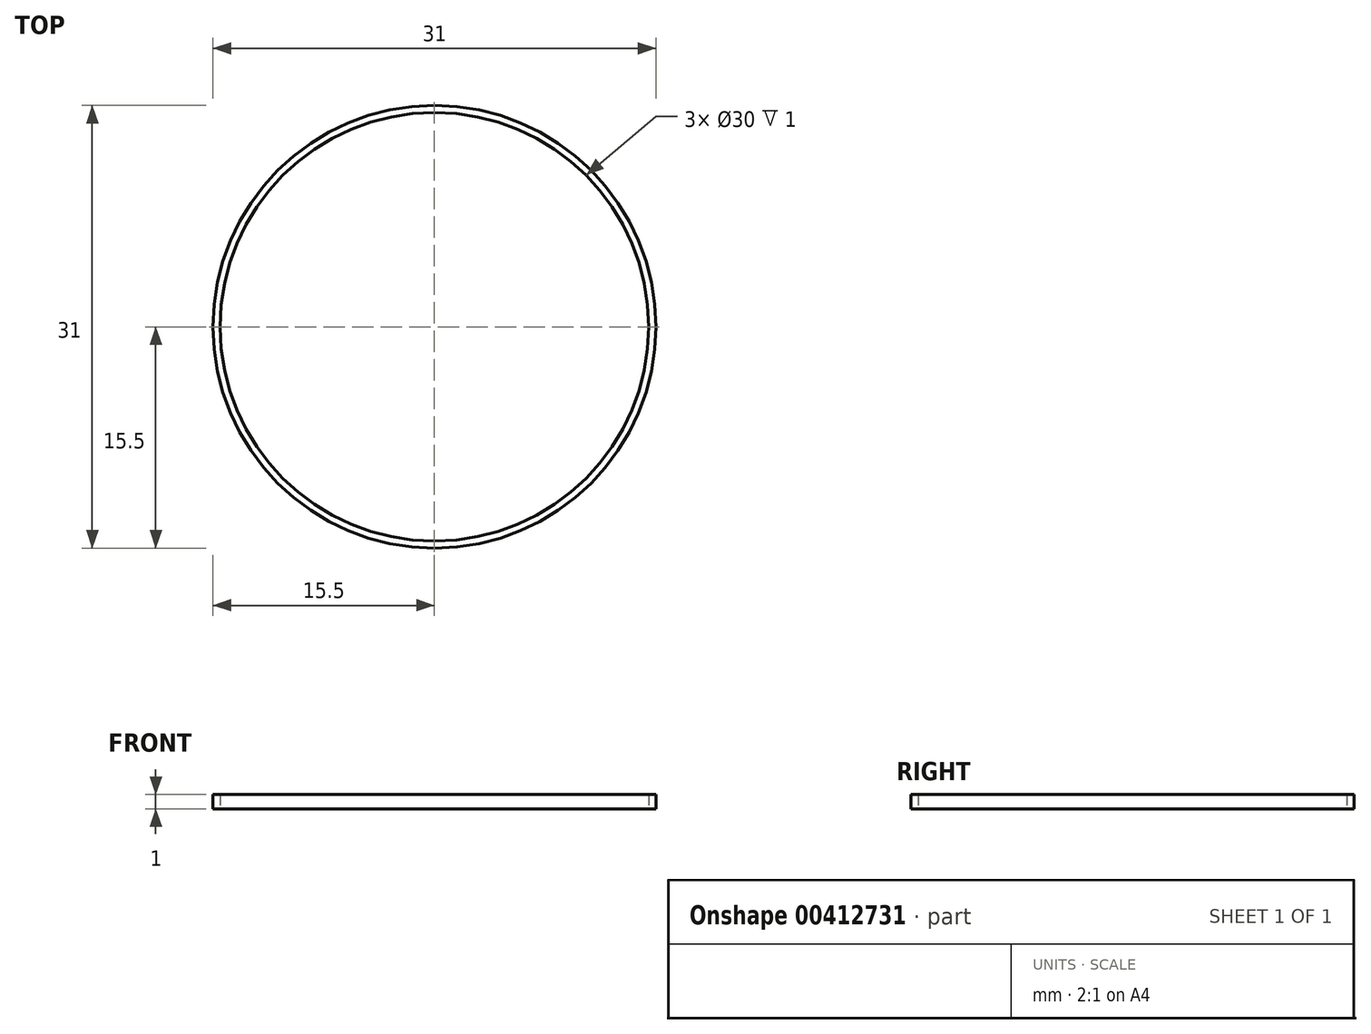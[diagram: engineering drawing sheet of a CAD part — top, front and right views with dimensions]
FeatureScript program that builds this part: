
annotation { "Feature Type Name" : "Feature", "Feature Type Description" : "" }
export const myFeature = defineFeature(function(context is Context, id is Id, definition is map)
    precondition{}
    {
        {
            var Q0;
            Q0=qCreatedBy(makeId("Top.planeOp"),FACE);
            var sketch = newSketch(context, id + "F0", { "sketchPlane" : qUnion([Q0])});
            skCircle(sketch, "E0", {"center": v(0, 0) * mm, "radius": 15 * mm});
            skCircle(sketch, "E1", {"center": v(0, 0) * mm, "radius": 15.5 * mm});
            skSolve(sketch);
        }
        {
            var Q0;
            Q0=makeQuery(id+"F0.imprint","IMPRINT",FACE,{"disambiguationData":[TD([[makeQuery(id+"F0.imprint","IMPRINT",EDGE,{"derivedFrom":sQuery(id+"F0.wireOp",EDGE,"E0")}),-1.0]])]});
            extrude(context, id + "F1", {"entities" : qUnion([Q0]), "depth" : 1 * mm, "offsetDistance" : 25 * mm});
        }
    });
